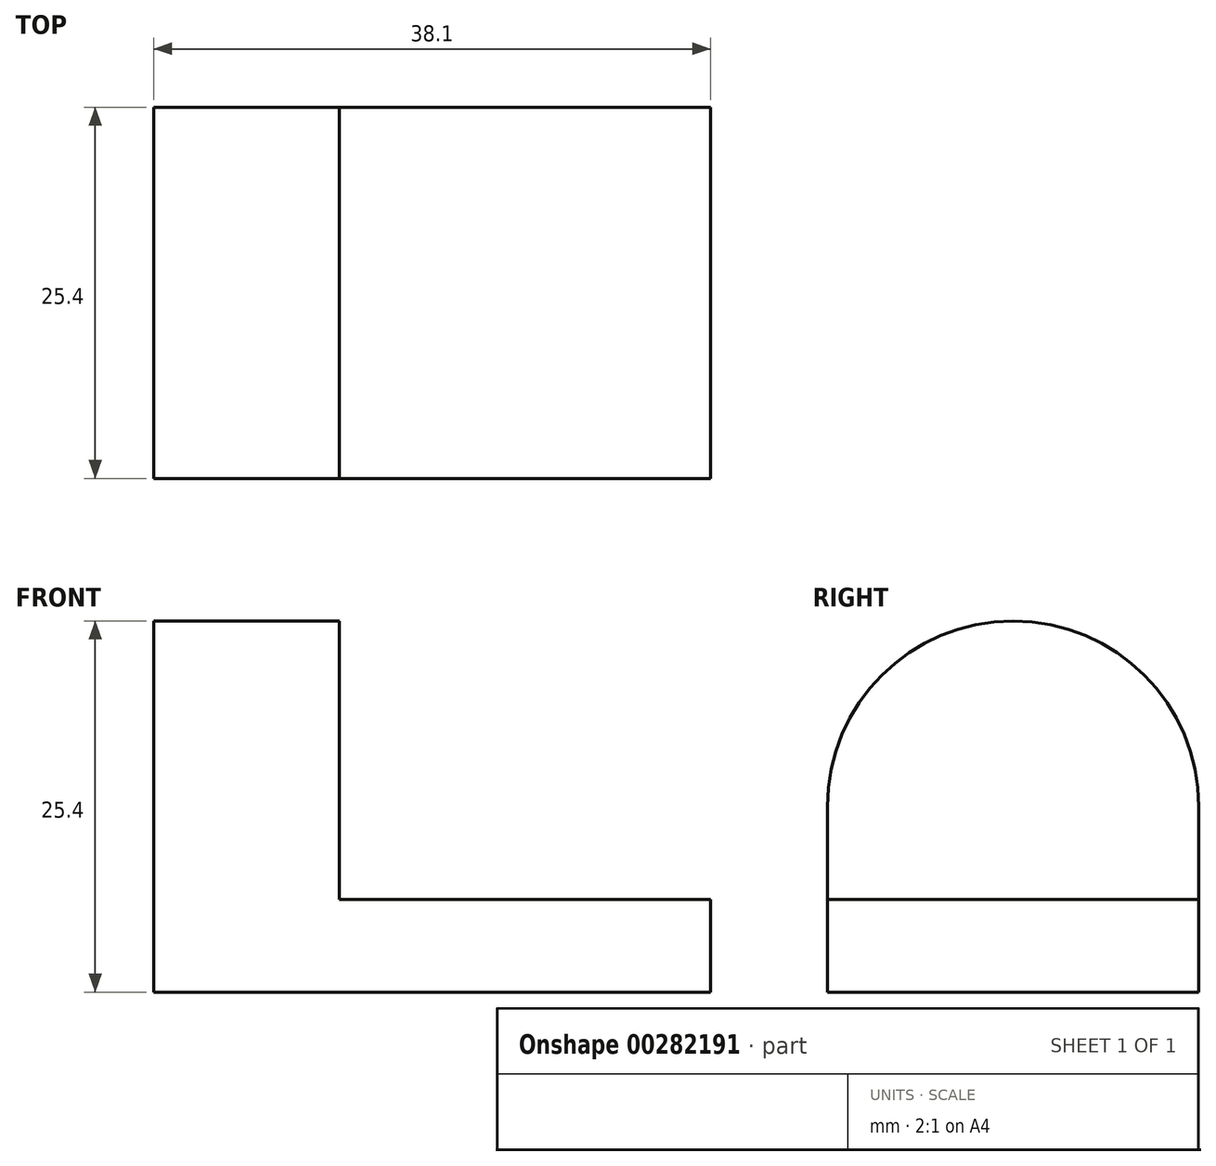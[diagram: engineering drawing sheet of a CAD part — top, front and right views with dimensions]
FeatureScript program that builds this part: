
annotation { "Feature Type Name" : "Feature", "Feature Type Description" : "" }
export const myFeature = defineFeature(function(context is Context, id is Id, definition is map)
    precondition{}
    {
        {
            var Q0;
            Q0=qCreatedBy(makeId("Front.planeOp"),FACE);
            var sketch = newSketch(context, id + "F0", { "sketchPlane" : qUnion([Q0])});
            skLineSegment(sketch, "E0", {"start": v(0, 0) * mm, "end": v(38.1, 0) * mm});
            skLineSegment(sketch, "E1", {"start": v(38.1, 0) * mm, "end": v(38.1, 6.35) * mm});
            skLineSegment(sketch, "E2", {"start": v(38.1, 6.35) * mm, "end": v(12.7, 6.35) * mm});
            skLineSegment(sketch, "E3", {"start": v(12.7, 6.35) * mm, "end": v(12.7, 12.7) * mm});
            skLineSegment(sketch, "E4", {"start": v(12.7, 12.7) * mm, "end": v(0, 12.7) * mm});
            skLineSegment(sketch, "E5", {"start": v(0, 12.7) * mm, "end": v(0, 0) * mm});
            skSolve(sketch);
        }
        {
            var Q0;
            Q0=makeQuery(id+"F0.imprint","IMPRINT",FACE,{"disambiguationData":[TD([[makeQuery(id+"F0.imprint","IMPRINT",EDGE,{"derivedFrom":sQuery(id+"F0.wireOp",EDGE,"E0")}),1.0]])]});
            extrude(context, id + "F1", {"entities" : qUnion([Q0]), "depth" : 25.4 * mm});
        }
        {
            var Q0;
            Q0=makeQuery(id+"F1.opExtrude","SWEPT_FACE",FACE,{"disambiguationData":[OSD([sQuery(id+"F0.wireOp",EDGE,"E3")])]});
            var sketch = newSketch(context, id + "F2", { "sketchPlane" : qUnion([Q0])});
            skArc(sketch, "E6", {"start": v(0, 12.7) * mm, "mid": v(-12.7, 25.4) * mm, "end": v(-25.4, 12.7) * mm});
            skSolve(sketch);
        }
        {
            var Q0;
            Q0=makeQuery(id+"F2.imprint","IMPRINT",FACE,{"disambiguationData":[TD([[makeQuery(id+"F2.imprint","IMPRINT",EDGE,{"derivedFrom":sQuery(id+"F2.wireOp",EDGE,"E6")}),1.0]])]});
            extrude(context, id + "F3", {"entities" : qUnion([Q0]), "operationType" : NewBodyOperationType.ADD, "oppositeDirection" : true, "depth" : 12.7 * mm});
        }
    });
